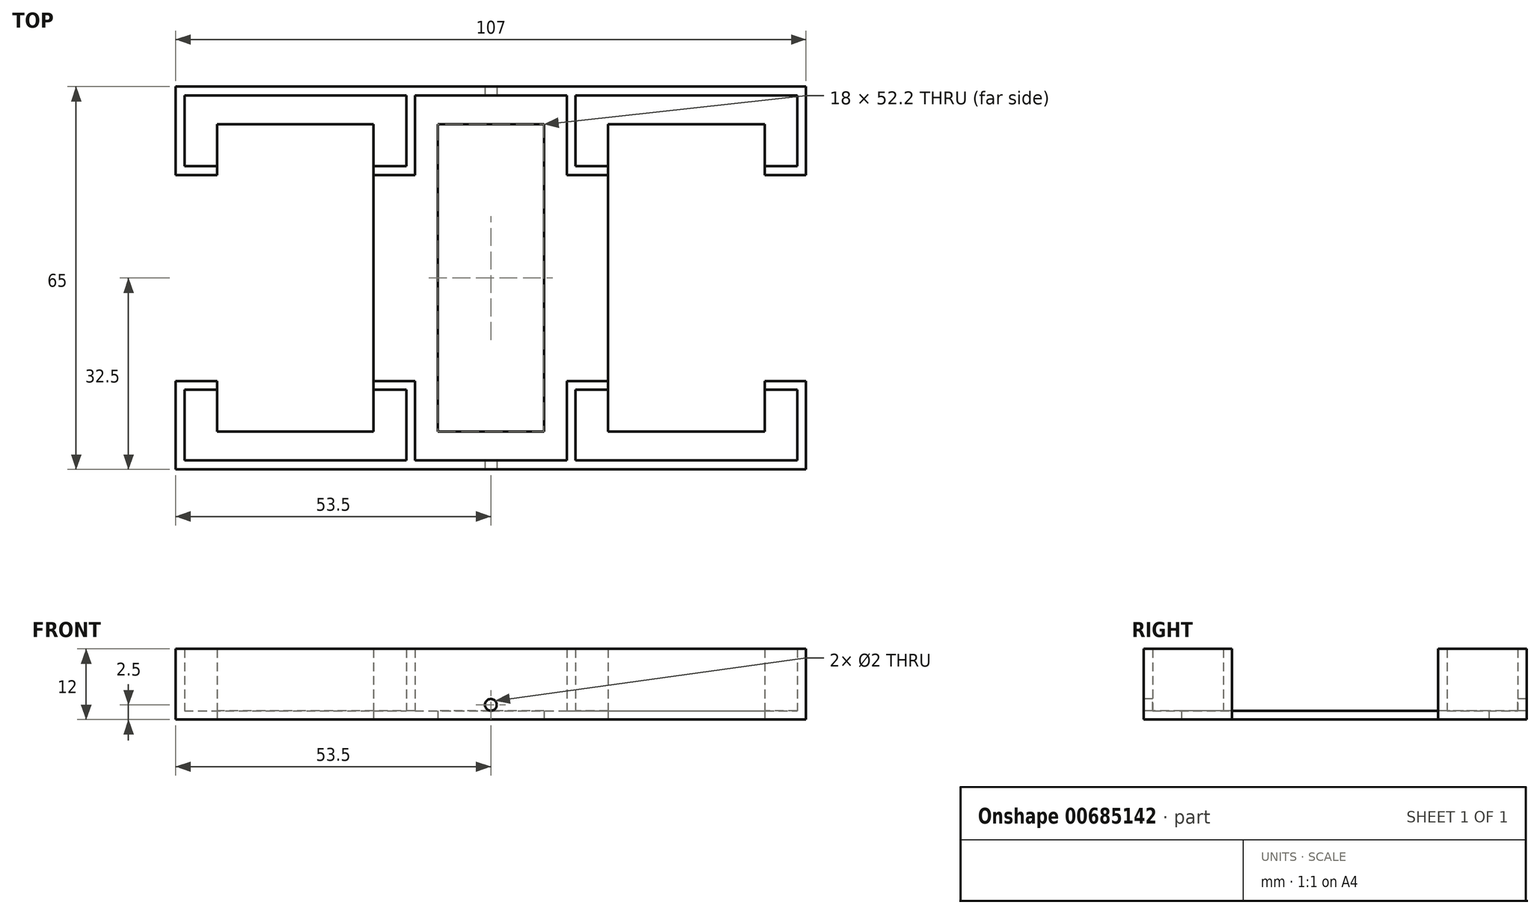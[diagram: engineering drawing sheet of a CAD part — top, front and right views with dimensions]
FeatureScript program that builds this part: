
annotation { "Feature Type Name" : "Feature", "Feature Type Description" : "" }
export const myFeature = defineFeature(function(context is Context, id is Id, definition is map)
    precondition{}
    {
        {
            var Q0;
            Q0=qCreatedBy(makeId("Top.planeOp"),FACE);
            var sketch = newSketch(context, id + "F0", { "sketchPlane" : qUnion([Q0])});
            skLineSegment(sketch, "E0", {"start": v(0, 32.5) * mm, "end": v(-53.5, 32.5) * mm});
            skLineSegment(sketch, "E1", {"start": v(-53.5, 32.5) * mm, "end": v(-53.5, 17.5) * mm});
            skLineSegment(sketch, "E2", {"start": v(-53.5, 17.5) * mm, "end": v(-46.5, 17.5) * mm});
            skLineSegment(sketch, "E3", {"start": v(-46.5, 17.5) * mm, "end": v(-46.5, 0) * mm});
            skLineSegment(sketch, "E4.MirrorCS", {"start": v(0, -32.5) * mm, "end": v(-53.5, -32.5) * mm});
            skLineSegment(sketch, "E5.MirrorCS", {"start": v(-53.5, -32.5) * mm, "end": v(-53.5, -17.5) * mm});
            skLineSegment(sketch, "E6.MirrorCS", {"start": v(-53.5, -17.5) * mm, "end": v(-46.5, -17.5) * mm});
            skLineSegment(sketch, "E7.MirrorCS", {"start": v(-46.5, -17.5) * mm, "end": v(-46.5, 0) * mm});
            skLineSegment(sketch, "E8.MirrorCS", {"start": v(0, 32.5) * mm, "end": v(53.5, 32.5) * mm});
            skLineSegment(sketch, "E9.MirrorCS", {"start": v(53.5, 32.5) * mm, "end": v(53.5, 17.5) * mm});
            skLineSegment(sketch, "E10.MirrorCS", {"start": v(53.5, 17.5) * mm, "end": v(46.5, 17.5) * mm});
            skLineSegment(sketch, "E11.MirrorCS", {"start": v(46.5, 17.5) * mm, "end": v(46.5, 0) * mm});
            skLineSegment(sketch, "E12.MirrorCS", {"start": v(46.5, -17.5) * mm, "end": v(46.5, 0) * mm});
            skLineSegment(sketch, "E13.MirrorCS", {"start": v(53.5, -17.5) * mm, "end": v(46.5, -17.5) * mm});
            skLineSegment(sketch, "E14.MirrorCS", {"start": v(53.5, -32.5) * mm, "end": v(53.5, -17.5) * mm});
            skLineSegment(sketch, "E15.MirrorCS", {"start": v(0, -32.5) * mm, "end": v(53.5, -32.5) * mm});
            skSolve(sketch);
        }
        {
            var Q0;
            Q0=makeQuery(id+"F0.imprint","IMPRINT",FACE,{"disambiguationData":[TD([[makeQuery(id+"F0.imprint","IMPRINT",EDGE,{"derivedFrom":sQuery(id+"F0.wireOp",EDGE,"E0")}),1.0]])]});
            extrude(context, id + "F1", {"entities" : qUnion([Q0]), "depth" : 12 * mm, "offsetDistance" : 25 * mm});
        }
        {
            var Q0;
            Q0=makeQuery(id+"F1.opExtrude","CAP_FACE",FACE,{"disambiguationData":[OSD([sQuery(id+"F0.wireOp",EDGE,"E0"),sQuery(id+"F0.wireOp",EDGE,"E1"),sQuery(id+"F0.wireOp",EDGE,"E2"),sQuery(id+"F0.wireOp",EDGE,"E3"),sQuery(id+"F0.wireOp",EDGE,"E4.MirrorCS"),sQuery(id+"F0.wireOp",EDGE,"E5.MirrorCS"),sQuery(id+"F0.wireOp",EDGE,"E6.MirrorCS"),sQuery(id+"F0.wireOp",EDGE,"E7.MirrorCS"),sQuery(id+"F0.wireOp",EDGE,"E8.MirrorCS"),sQuery(id+"F0.wireOp",EDGE,"E9.MirrorCS"),sQuery(id+"F0.wireOp",EDGE,"E10.MirrorCS"),sQuery(id+"F0.wireOp",EDGE,"E11.MirrorCS"),sQuery(id+"F0.wireOp",EDGE,"E12.MirrorCS"),sQuery(id+"F0.wireOp",EDGE,"E13.MirrorCS"),sQuery(id+"F0.wireOp",EDGE,"E14.MirrorCS"),sQuery(id+"F0.wireOp",EDGE,"E15.MirrorCS")])],"isStart":false});
            shell(context, id + "F2", {"entities" : qUnion([Q0]), "thickness" : 1.5 * mm});
        }
        {
            var Q0;
            Q0=makeQuery(id+"F1.opExtrude","SWEPT_FACE",FACE,{"disambiguationData":[OSD([sQuery(id+"F0.wireOp",EDGE,"E4.MirrorCS"),sQuery(id+"F0.wireOp",EDGE,"E15.MirrorCS")])]});
            var sketch = newSketch(context, id + "F3", { "sketchPlane" : qUnion([Q0])});
            skCircle(sketch, "E16", {"center": v(0, 2.5) * mm, "radius": 1 * mm});
            skSolve(sketch);
        }
        {
            var Q0;
            Q0=makeQuery(id+"F3.imprint","IMPRINT",FACE,{"disambiguationData":[TD([[makeQuery(id+"F3.imprint","IMPRINT",EDGE,{"derivedFrom":sQuery(id+"F3.wireOp",EDGE,"E16")}),1.0]])]});
            extrude(context, id + "F4", {"entities" : qUnion([Q0]), "operationType" : NewBodyOperationType.REMOVE, "oppositeDirection" : true, "depth" : 70 * mm, "offsetDistance" : 25 * mm});
        }
        {
            var Q0;
            Q0=makeQuery(id+"F1.opExtrude","CAP_FACE",FACE,{"disambiguationData":[OSD([sQuery(id+"F0.wireOp",EDGE,"E0"),sQuery(id+"F0.wireOp",EDGE,"E1"),sQuery(id+"F0.wireOp",EDGE,"E2"),sQuery(id+"F0.wireOp",EDGE,"E3"),sQuery(id+"F0.wireOp",EDGE,"E4.MirrorCS"),sQuery(id+"F0.wireOp",EDGE,"E5.MirrorCS"),sQuery(id+"F0.wireOp",EDGE,"E6.MirrorCS"),sQuery(id+"F0.wireOp",EDGE,"E7.MirrorCS"),sQuery(id+"F0.wireOp",EDGE,"E8.MirrorCS"),sQuery(id+"F0.wireOp",EDGE,"E9.MirrorCS"),sQuery(id+"F0.wireOp",EDGE,"E10.MirrorCS"),sQuery(id+"F0.wireOp",EDGE,"E11.MirrorCS"),sQuery(id+"F0.wireOp",EDGE,"E12.MirrorCS"),sQuery(id+"F0.wireOp",EDGE,"E13.MirrorCS"),sQuery(id+"F0.wireOp",EDGE,"E14.MirrorCS"),sQuery(id+"F0.wireOp",EDGE,"E15.MirrorCS")])],"isStart":true});
            var sketch = newSketch(context, id + "F5", { "sketchPlane" : qUnion([Q0])});
            skLineSegment(sketch, "E17.bottom", {"start": v(-46.5, 26.1) * mm, "end": v(-19.9, 26.1) * mm});
            skLineSegment(sketch, "E17.top", {"start": v(-46.5, -26.1) * mm, "end": v(-19.9, -26.1) * mm});
            skLineSegment(sketch, "E17.left", {"start": v(-46.5, 26.1) * mm, "end": v(-46.5, -26.1) * mm});
            skLineSegment(sketch, "E17.right", {"start": v(-19.9, 26.1) * mm, "end": v(-19.9, -26.1) * mm});
            skLineSegment(sketch, "E18.MirrorCS", {"start": v(46.5, 26.1) * mm, "end": v(19.9, 26.1) * mm});
            skLineSegment(sketch, "E19.MirrorCS", {"start": v(46.5, 26.1) * mm, "end": v(46.5, -26.1) * mm});
            skLineSegment(sketch, "E20.MirrorCS", {"start": v(19.9, 26.1) * mm, "end": v(19.9, -26.1) * mm});
            skLineSegment(sketch, "E21.MirrorCS", {"start": v(46.5, -26.1) * mm, "end": v(19.9, -26.1) * mm});
            skLineSegment(sketch, "E22.bottom", {"start": v(-9, 26.1) * mm, "end": v(9, 26.1) * mm});
            skLineSegment(sketch, "E22.top", {"start": v(-9, -26.1) * mm, "end": v(9, -26.1) * mm});
            skLineSegment(sketch, "E22.left", {"start": v(-9, 26.1) * mm, "end": v(-9, -26.1) * mm});
            skLineSegment(sketch, "E22.right", {"start": v(9, 26.1) * mm, "end": v(9, -26.1) * mm});
            skSolve(sketch);
        }
        {
            var Q0;
            {var subQ3=sQuery(id+"F5.wireOp",EDGE,"E17.bottom");Q0=makeQuery(id+"F5.imprint","IMPRINT",FACE,{"disambiguationData":[TD([[makeQuery(id+"F5.imprint","IMPRINT",EDGE,{"derivedFrom":subQ3}),-1.0]])]});}
            var Q1;
            Q1=makeQuery(id+"F5.imprint","IMPRINT",FACE,{"disambiguationData":[TD([[makeQuery(id+"F5.imprint","IMPRINT",EDGE,{"derivedFrom":sQuery(id+"F5.wireOp",EDGE,"E22.bottom")}),-1.0]])]});
            var Q2;
            {var subQ4=sQuery(id+"F5.wireOp",EDGE,"E18.MirrorCS");Q2=makeQuery(id+"F5.imprint","IMPRINT",FACE,{"disambiguationData":[TD([[makeQuery(id+"F5.imprint","IMPRINT",EDGE,{"derivedFrom":subQ4}),1.0]])]});}
            extrude(context, id + "F6", {"entities" : qUnion([Q0, Q1, Q2]), "operationType" : NewBodyOperationType.REMOVE, "oppositeDirection" : true, "depth" : 25 * mm, "offsetDistance" : 25 * mm});
        }
        {
            var Q0;
            {var subQ0=sQuery(id+"F0.wireOp",EDGE,"E9.MirrorCS");var subQ1=sQuery(id+"F0.wireOp",EDGE,"E2");var subQ2=sQuery(id+"F0.wireOp",EDGE,"E1");var subQ3=sQuery(id+"F0.wireOp",EDGE,"E8.MirrorCS");var subQ4=sQuery(id+"F0.wireOp",EDGE,"E0");var subQ5=sQuery(id+"F0.wireOp",EDGE,"E10.MirrorCS");Q0=makeQuery(id+"F6.boolean.opBoolean","SPLIT",FACE,{"disambiguationData":[TD([makeQuery(id+"F1.opExtrude","SWEPT_FACE",FACE,{"disambiguationData":[OSD([subQ2])]})])],"derivedFrom":makeQuery(id+"F1.opExtrude","CAP_FACE",FACE,{"disambiguationData":[OSD([subQ4,subQ2,subQ1,sQuery(id+"F0.wireOp",EDGE,"E3"),sQuery(id+"F0.wireOp",EDGE,"E4.MirrorCS"),sQuery(id+"F0.wireOp",EDGE,"E5.MirrorCS"),sQuery(id+"F0.wireOp",EDGE,"E6.MirrorCS"),sQuery(id+"F0.wireOp",EDGE,"E7.MirrorCS"),subQ3,subQ0,subQ5,sQuery(id+"F0.wireOp",EDGE,"E11.MirrorCS"),sQuery(id+"F0.wireOp",EDGE,"E12.MirrorCS"),sQuery(id+"F0.wireOp",EDGE,"E13.MirrorCS"),sQuery(id+"F0.wireOp",EDGE,"E14.MirrorCS"),sQuery(id+"F0.wireOp",EDGE,"E15.MirrorCS")])],"isStart":false})});}
            var sketch = newSketch(context, id + "F7", { "sketchPlane" : qUnion([Q0])});
            skLineSegment(sketch, "E23.bottom", {"start": v(-53.5, 27.15) * mm, "end": v(-52, 27.15) * mm});
            skLineSegment(sketch, "E23.top", {"start": v(-53.5, 21.65) * mm, "end": v(-52, 21.65) * mm});
            skLineSegment(sketch, "E23.left", {"start": v(-53.5, 27.15) * mm, "end": v(-53.5, 21.65) * mm});
            skLineSegment(sketch, "E23.right", {"start": v(-52, 27.15) * mm, "end": v(-52, 21.65) * mm});
            skLineSegment(sketch, "E24.MirrorCS", {"start": v(53.5, 27.15) * mm, "end": v(52, 27.15) * mm});
            skLineSegment(sketch, "E25.MirrorCS", {"start": v(53.5, 27.15) * mm, "end": v(53.5, 21.65) * mm});
            skLineSegment(sketch, "E26.MirrorCS", {"start": v(52, 27.15) * mm, "end": v(52, 21.65) * mm});
            skLineSegment(sketch, "E27.MirrorCS", {"start": v(53.5, 21.65) * mm, "end": v(52, 21.65) * mm});
            skLineSegment(sketch, "E28.MirrorCS", {"start": v(-53.5, -27.15) * mm, "end": v(-53.5, -21.65) * mm});
            skLineSegment(sketch, "E29.MirrorCS", {"start": v(-53.5, -27.15) * mm, "end": v(-52, -27.15) * mm});
            skLineSegment(sketch, "E30.MirrorCS", {"start": v(-52, -27.15) * mm, "end": v(-52, -21.65) * mm});
            skLineSegment(sketch, "E31.MirrorCS", {"start": v(-53.5, -21.65) * mm, "end": v(-52, -21.65) * mm});
            skLineSegment(sketch, "E32.MirrorCS", {"start": v(53.5, -27.15) * mm, "end": v(52, -27.15) * mm});
            skLineSegment(sketch, "E33.MirrorCS", {"start": v(52, -27.15) * mm, "end": v(52, -21.65) * mm});
            skLineSegment(sketch, "E34.MirrorCS", {"start": v(53.5, -27.15) * mm, "end": v(53.5, -21.65) * mm});
            skLineSegment(sketch, "E35.MirrorCS", {"start": v(53.5, -21.65) * mm, "end": v(52, -21.65) * mm});
            skSolve(sketch);
        }
        {
            var Q0;
            Q0=makeQuery(id+"F2.opShell","OFFSET_FACE",FACE,{"disambiguationData":[OSD([sQuery(id+"F0.wireOp",EDGE,"E0"),sQuery(id+"F0.wireOp",EDGE,"E1"),sQuery(id+"F0.wireOp",EDGE,"E2"),sQuery(id+"F0.wireOp",EDGE,"E3"),sQuery(id+"F0.wireOp",EDGE,"E4.MirrorCS"),sQuery(id+"F0.wireOp",EDGE,"E5.MirrorCS"),sQuery(id+"F0.wireOp",EDGE,"E6.MirrorCS"),sQuery(id+"F0.wireOp",EDGE,"E7.MirrorCS"),sQuery(id+"F0.wireOp",EDGE,"E8.MirrorCS"),sQuery(id+"F0.wireOp",EDGE,"E9.MirrorCS"),sQuery(id+"F0.wireOp",EDGE,"E10.MirrorCS"),sQuery(id+"F0.wireOp",EDGE,"E11.MirrorCS"),sQuery(id+"F0.wireOp",EDGE,"E12.MirrorCS"),sQuery(id+"F0.wireOp",EDGE,"E13.MirrorCS"),sQuery(id+"F0.wireOp",EDGE,"E14.MirrorCS"),sQuery(id+"F0.wireOp",EDGE,"E15.MirrorCS")])]});
            var sketch = newSketch(context, id + "F8", { "sketchPlane" : qUnion([Q0])});
            skLineSegment(sketch, "E36", {"start": v(-19.9, -19) * mm, "end": v(-14.36, -19) * mm});
            skLineSegment(sketch, "E37", {"start": v(-14.36, -19) * mm, "end": v(-14.36, -31) * mm});
            skLineSegment(sketch, "E38", {"start": v(-14.36, -31) * mm, "end": v(-12.9, -31) * mm});
            skLineSegment(sketch, "E39", {"start": v(-12.9, -31) * mm, "end": v(-12.9, -17.5) * mm});
            skLineSegment(sketch, "E40", {"start": v(-12.9, -17.5) * mm, "end": v(-19.9, -17.5) * mm});
            skLineSegment(sketch, "E41", {"start": v(-19.9, -17.5) * mm, "end": v(-19.9, -19) * mm});
            skLineSegment(sketch, "E42.MirrorCS", {"start": v(12.9, -17.5) * mm, "end": v(19.9, -17.5) * mm});
            skLineSegment(sketch, "E43.MirrorCS", {"start": v(19.9, -17.5) * mm, "end": v(19.9, -19) * mm});
            skLineSegment(sketch, "E44.MirrorCS", {"start": v(19.9, -19) * mm, "end": v(14.36, -19) * mm});
            skLineSegment(sketch, "E45.MirrorCS", {"start": v(14.36, -19) * mm, "end": v(14.36, -31) * mm});
            skLineSegment(sketch, "E46.MirrorCS", {"start": v(14.36, -31) * mm, "end": v(12.9, -31) * mm});
            skLineSegment(sketch, "E47.MirrorCS", {"start": v(12.9, -31) * mm, "end": v(12.9, -17.5) * mm});
            skLineSegment(sketch, "E48.MirrorCS", {"start": v(-12.9, 17.5) * mm, "end": v(-19.9, 17.5) * mm});
            skLineSegment(sketch, "E49.MirrorCS", {"start": v(-19.9, 17.5) * mm, "end": v(-19.9, 19) * mm});
            skLineSegment(sketch, "E50.MirrorCS", {"start": v(-19.9, 19) * mm, "end": v(-14.36, 19) * mm});
            skLineSegment(sketch, "E51.MirrorCS", {"start": v(-14.36, 19) * mm, "end": v(-14.36, 31) * mm});
            skLineSegment(sketch, "E52.MirrorCS", {"start": v(-14.36, 31) * mm, "end": v(-12.9, 31) * mm});
            skLineSegment(sketch, "E53.MirrorCS", {"start": v(-12.9, 31) * mm, "end": v(-12.9, 17.5) * mm});
            skLineSegment(sketch, "E54.MirrorCS", {"start": v(12.9, 17.5) * mm, "end": v(19.9, 17.5) * mm});
            skLineSegment(sketch, "E55.MirrorCS", {"start": v(19.9, 17.5) * mm, "end": v(19.9, 19) * mm});
            skLineSegment(sketch, "E56.MirrorCS", {"start": v(19.9, 19) * mm, "end": v(14.36, 19) * mm});
            skLineSegment(sketch, "E57.MirrorCS", {"start": v(14.36, 19) * mm, "end": v(14.36, 31) * mm});
            skLineSegment(sketch, "E58.MirrorCS", {"start": v(14.36, 31) * mm, "end": v(12.9, 31) * mm});
            skLineSegment(sketch, "E59.MirrorCS", {"start": v(12.9, 31) * mm, "end": v(12.9, 17.5) * mm});
            skSolve(sketch);
        }
        {
            var Q0;
            Q0=makeQuery(id+"F8.imprint","IMPRINT",FACE,{"disambiguationData":[TD([[makeQuery(id+"F8.imprint","IMPRINT",EDGE,{"derivedFrom":sQuery(id+"F8.wireOp",EDGE,"E48.MirrorCS")}),-1.0]])]});
            var Q1;
            Q1=makeQuery(id+"F8.imprint","IMPRINT",FACE,{"disambiguationData":[TD([[makeQuery(id+"F8.imprint","IMPRINT",EDGE,{"derivedFrom":sQuery(id+"F8.wireOp",EDGE,"E54.MirrorCS")}),1.0]])]});
            var Q2;
            Q2=makeQuery(id+"F8.imprint","IMPRINT",FACE,{"disambiguationData":[TD([[makeQuery(id+"F8.imprint","IMPRINT",EDGE,{"derivedFrom":sQuery(id+"F8.wireOp",EDGE,"E42.MirrorCS")}),-1.0]])]});
            var Q3;
            Q3=makeQuery(id+"F8.imprint","IMPRINT",FACE,{"disambiguationData":[TD([[makeQuery(id+"F8.imprint","IMPRINT",EDGE,{"derivedFrom":sQuery(id+"F8.wireOp",EDGE,"E36")}),1.0]])]});
            extrude(context, id + "F9", {"entities" : qUnion([Q0, Q1, Q2, Q3]), "operationType" : NewBodyOperationType.ADD, "depth" : 10.5 * mm, "offsetDistance" : 25 * mm});
        }
    });
